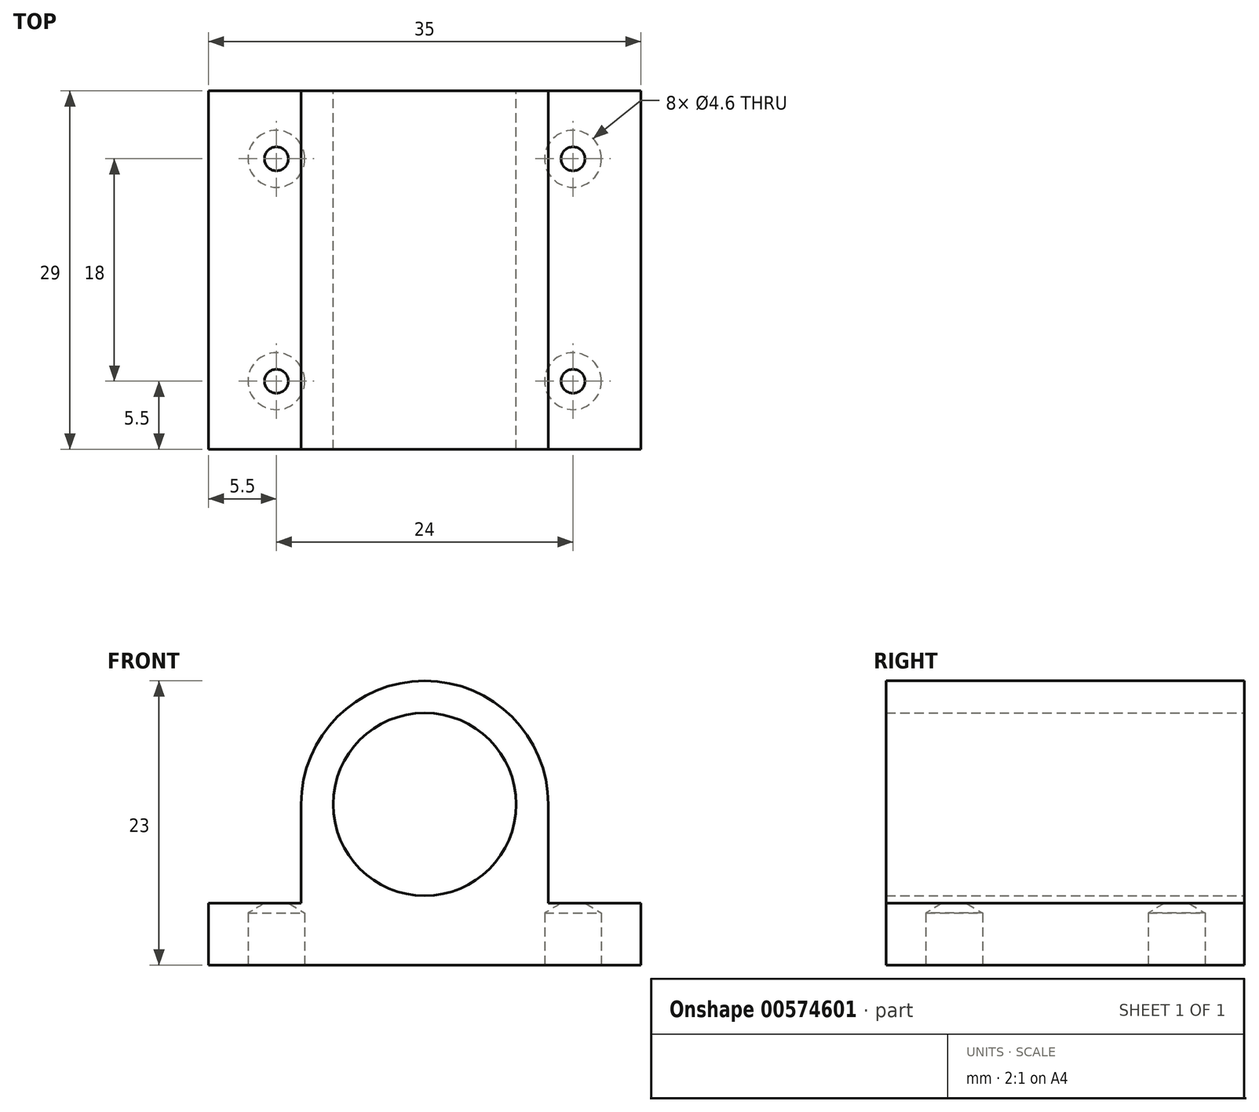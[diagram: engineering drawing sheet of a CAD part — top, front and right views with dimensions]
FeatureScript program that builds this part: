
annotation { "Feature Type Name" : "Feature", "Feature Type Description" : "" }
export const myFeature = defineFeature(function(context is Context, id is Id, definition is map)
    precondition{}
    {
        {
            var Q0;
            Q0=qCreatedBy(makeId("Front.planeOp"),FACE);
            var sketch = newSketch(context, id + "F0", { "sketchPlane" : qUnion([Q0])});
            skLineSegment(sketch, "E0", {"start": v(0, 0) * mm, "end": v(17.5, 0) * mm});
            skLineSegment(sketch, "E1", {"start": v(17.5, 0) * mm, "end": v(17.5, 5) * mm});
            skLineSegment(sketch, "E2", {"start": v(17.5, 5) * mm, "end": v(10, 5) * mm});
            skLineSegment(sketch, "E3.MirrorCS", {"start": v(-17.5, 5) * mm, "end": v(-10, 5) * mm});
            skLineSegment(sketch, "E4.MirrorCS", {"start": v(0, 0) * mm, "end": v(-17.5, 0) * mm});
            skLineSegment(sketch, "E5.MirrorCS", {"start": v(-17.5, 0) * mm, "end": v(-17.5, 5) * mm});
            skLineSegment(sketch, "E6", {"start": v(10, 5) * mm, "end": v(10, 13) * mm});
            skLineSegment(sketch, "E7", {"start": v(0, -6.19) * mm, "end": v(0, 32.8) * mm, "construction": true});
            skLineSegment(sketch, "E8.MirrorCS", {"start": v(-10, 5) * mm, "end": v(-10, 13) * mm});
            skLineSegment(sketch, "E9", {"start": v(0, 20.4) * mm, "end": v(0, 23) * mm});
            skArc(sketch, "E10", {"start": v(0, 23) * mm, "mid": v(7.07, 20.07) * mm, "end": v(10, 13) * mm});
            skArc(sketch, "E11", {"start": v(0, 20.4) * mm, "mid": v(7.4, 13) * mm, "end": v(0, 5.6) * mm});
            skArc(sketch, "E12.MirrorCS", {"start": v(0, 23) * mm, "mid": v(-7.07, 20.07) * mm, "end": v(-10, 13) * mm});
            skArc(sketch, "E13.MirrorCS", {"start": v(0, 20.4) * mm, "mid": v(-7.4, 13) * mm, "end": v(0, 5.6) * mm});
            skSolve(sketch);
        }
        {
            var Q0;
            Q0=makeQuery(id+"F0.imprint","IMPRINT",FACE,{"disambiguationData":[TD([[makeQuery(id+"F0.imprint","IMPRINT",EDGE,{"derivedFrom":sQuery(id+"F0.wireOp",EDGE,"E0")}),1.0]])]});
            extrude(context, id + "F1", {"entities" : qUnion([Q0]), "depth" : 29 * mm, "offsetDistance" : 25 * mm});
        }
        {
            var Q0;
            Q0=makeQuery(id+"F1.opExtrude","SWEPT_FACE",FACE,{"disambiguationData":[OSD([sQuery(id+"F0.wireOp",EDGE,"E0"),sQuery(id+"F0.wireOp",EDGE,"E4.MirrorCS")])]});
            var sketch = newSketch(context, id + "F2", { "sketchPlane" : qUnion([Q0])});
            skCircle(sketch, "E14", {"center": v(-12, 23.5) * mm, "radius": 1.75 * mm});
            skLineSegment(sketch, "E15", {"start": v(0, 29) * mm, "end": v(0, -3.36) * mm, "construction": true});
            skCircle(sketch, "E16.MirrorC", {"center": v(12, 23.5) * mm, "radius": 1.75 * mm});
            skLineSegment(sketch, "E17", {"start": v(-17.5, 14.5) * mm, "end": v(22.83, 14.5) * mm, "construction": true});
            skCircle(sketch, "E18.MirrorC", {"center": v(-12, 5.5) * mm, "radius": 1.75 * mm});
            skCircle(sketch, "E19.MirrorC", {"center": v(12, 5.5) * mm, "radius": 1.75 * mm});
            skSolve(sketch);
        }
        {
            var Q0;
            Q0=sQuery(id+"F2.wireOp",VERTEX,"E14.center");
            var Q1;
            Q1=sQuery(id+"F2.wireOp",VERTEX,"E16.MirrorC.center");
            var Q2;
            Q2=sQuery(id+"F2.wireOp",VERTEX,"E18.MirrorC.center");
            var Q3;
            Q3=sQuery(id+"F2.wireOp",VERTEX,"E19.MirrorC.center");
            var Q4;
            Q4=makeQuery(id+"F1.opExtrude","SWEPT_BODY",BODY,{"disambiguationData":[OSD([sQuery(id+"F0.wireOp",EDGE,"E0"),sQuery(id+"F0.wireOp",EDGE,"E1"),sQuery(id+"F0.wireOp",EDGE,"E2"),sQuery(id+"F0.wireOp",EDGE,"Ly3XzaFO-MEAt-RE6F-LE8l-fyG6Mi8BUAm2"),sQuery(id+"F0.wireOp",EDGE,"3jlH0nAH-E49l-eZvV-lZ3N-rKZ6AzdrQb22"),sQuery(id+"F0.wireOp",EDGE,"yvDeuFeR-fRS9-B6Mu-2o3Q-hFL0JikA8Qs7"),sQuery(id+"F0.wireOp",EDGE,"E3.MirrorCS"),sQuery(id+"F0.wireOp",EDGE,"4d9fa47a-55e8-4596-9c28-741cee9445161.MirrorCS"),sQuery(id+"F0.wireOp",EDGE,"4d9fa47a-55e8-4596-9c28-741cee9445162.MirrorCS"),sQuery(id+"F0.wireOp",EDGE,"4d9fa47a-55e8-4596-9c28-741cee9445163.MirrorCS"),sQuery(id+"F0.wireOp",EDGE,"E4.MirrorCS"),sQuery(id+"F0.wireOp",EDGE,"E5.MirrorCS"),sQuery(id+"F0.wireOp",EDGE,"qFv9hw4z-pqMv-xcqi-xRy1-RO01PiSc1E5p")])]});
            hole(context, id + "F3", {"style" : HoleStyle.SIMPLE, "endStyle" : HoleEndStyle.BLIND, "holeDiameter" : 4.6 * mm, "holeDepth" : 4.2 * mm, "isTappedThrough" : true, "tappedDepth" : 12 * mm, "tapClearance" : 3, "locations" : qUnion([Q0, Q1, Q2, Q3]), "scope" : qUnion([Q4]), "majorDiameter" : 5 * mm});
        }
        {
            var Q0;
            Q0=makeQuery(id+"F1.opExtrude","SWEPT_BODY",BODY,{"disambiguationData":[OSD([sQuery(id+"F0.wireOp",EDGE,"E0"),sQuery(id+"F0.wireOp",EDGE,"E1"),sQuery(id+"F0.wireOp",EDGE,"E2"),sQuery(id+"F0.wireOp",EDGE,"E3.MirrorCS"),sQuery(id+"F0.wireOp",EDGE,"E4.MirrorCS"),sQuery(id+"F0.wireOp",EDGE,"E5.MirrorCS"),sQuery(id+"F0.wireOp",EDGE,"E6"),sQuery(id+"F0.wireOp",EDGE,"E8.MirrorCS"),sQuery(id+"F0.wireOp",EDGE,"E9"),sQuery(id+"F0.wireOp",EDGE,"E10"),sQuery(id+"F0.wireOp",EDGE,"E11"),sQuery(id+"F0.wireOp",EDGE,"E12.MirrorCS"),sQuery(id+"F0.wireOp",EDGE,"E9"),sQuery(id+"F0.wireOp",EDGE,"E13.MirrorCS")])]});
            transform(context, id + "F4", {"entities" : qUnion([Q0]), "transformType" : TransformType.TRANSLATION_3D, "dx" : 0 * mm, "dy" : 0 * mm, "dz" : 0 * mm, "makeCopy" : true});
        }
    });
